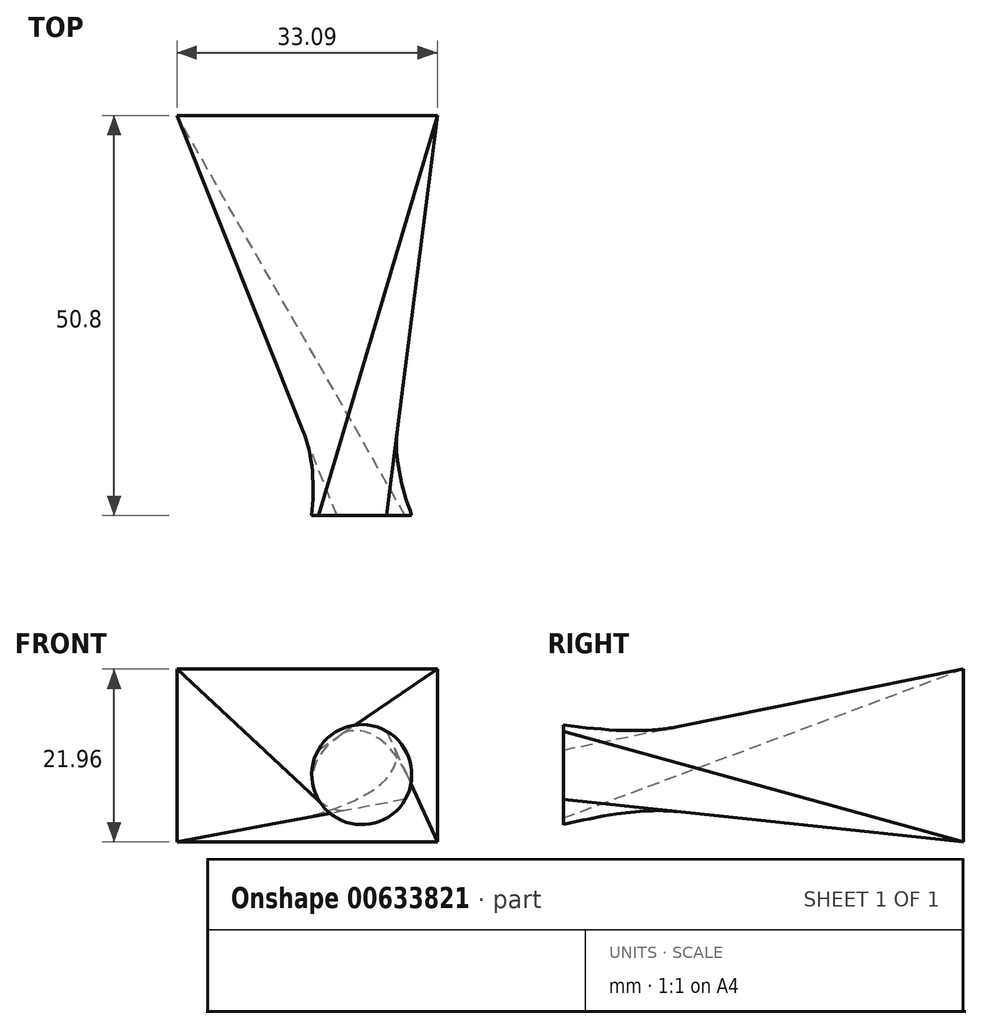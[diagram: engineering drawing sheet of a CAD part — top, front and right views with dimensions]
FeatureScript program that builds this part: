
annotation { "Feature Type Name" : "Feature", "Feature Type Description" : "" }
export const myFeature = defineFeature(function(context is Context, id is Id, definition is map)
    precondition{}
    {
        {
            var Q0;
            Q0=qCreatedBy(makeId("Front.planeOp"),FACE);
            var sketch = newSketch(context, id + "F0", { "sketchPlane" : qUnion([Q0])});
            skCircle(sketch, "E0", {"center": v(-25.4, 5.08) * mm, "radius": 6.35 * mm});
            skCircle(sketch, "E1", {"center": v(-22.33, -11.02) * mm, "radius": 5.6 * mm});
            skSolve(sketch);
        }
        {
            var Q0;
            Q0=qCreatedBy(makeId("Front.planeOp"),FACE);
            cPlane(context, id + "F1", {"entities" : qUnion([Q0]), "cplaneType" : CPlaneType.OFFSET, "offset" : 50.8 * mm, "oppositeDirection" : true, "width" : 152.4 * mm, "height" : 152.4 * mm});
        }
        {
            var Q0;
            Q0=qCreatedBy(id+"F1.planeOp",FACE);
            var sketch = newSketch(context, id + "F2", { "sketchPlane" : qUnion([Q0])});
            skLineSegment(sketch, "E2.bottom", {"start": v(-48.88, 18.5) * mm, "end": v(-15.8, 18.5) * mm});
            skLineSegment(sketch, "E2.top", {"start": v(-48.88, -3.46) * mm, "end": v(-15.8, -3.46) * mm});
            skLineSegment(sketch, "E2.left", {"start": v(-48.88, 18.5) * mm, "end": v(-48.88, -3.46) * mm});
            skLineSegment(sketch, "E2.right", {"start": v(-15.8, 18.5) * mm, "end": v(-15.8, -3.46) * mm});
            skSolve(sketch);
        }
        {
            var Q0;
            Q0=makeQuery(id+"F0.imprint","IMPRINT",FACE,{"disambiguationData":[TD([[makeQuery(id+"F0.imprint","IMPRINT",EDGE,{"derivedFrom":sQuery(id+"F0.wireOp",EDGE,"E0")}),1.0]])]});
            var Q1;
            Q1=makeQuery(id+"F2.imprint","IMPRINT",FACE,{"disambiguationData":[TD([[makeQuery(id+"F2.imprint","IMPRINT",EDGE,{"derivedFrom":sQuery(id+"F2.wireOp",EDGE,"E2.bottom")}),-1.0]])]});
            loft(context, id + "F3", {"sheetProfilesArray" : [{ "sheetProfileEntities" : qUnion([Q0]) }, { "sheetProfileEntities" : qUnion([Q1]) }]});
        }
    });
